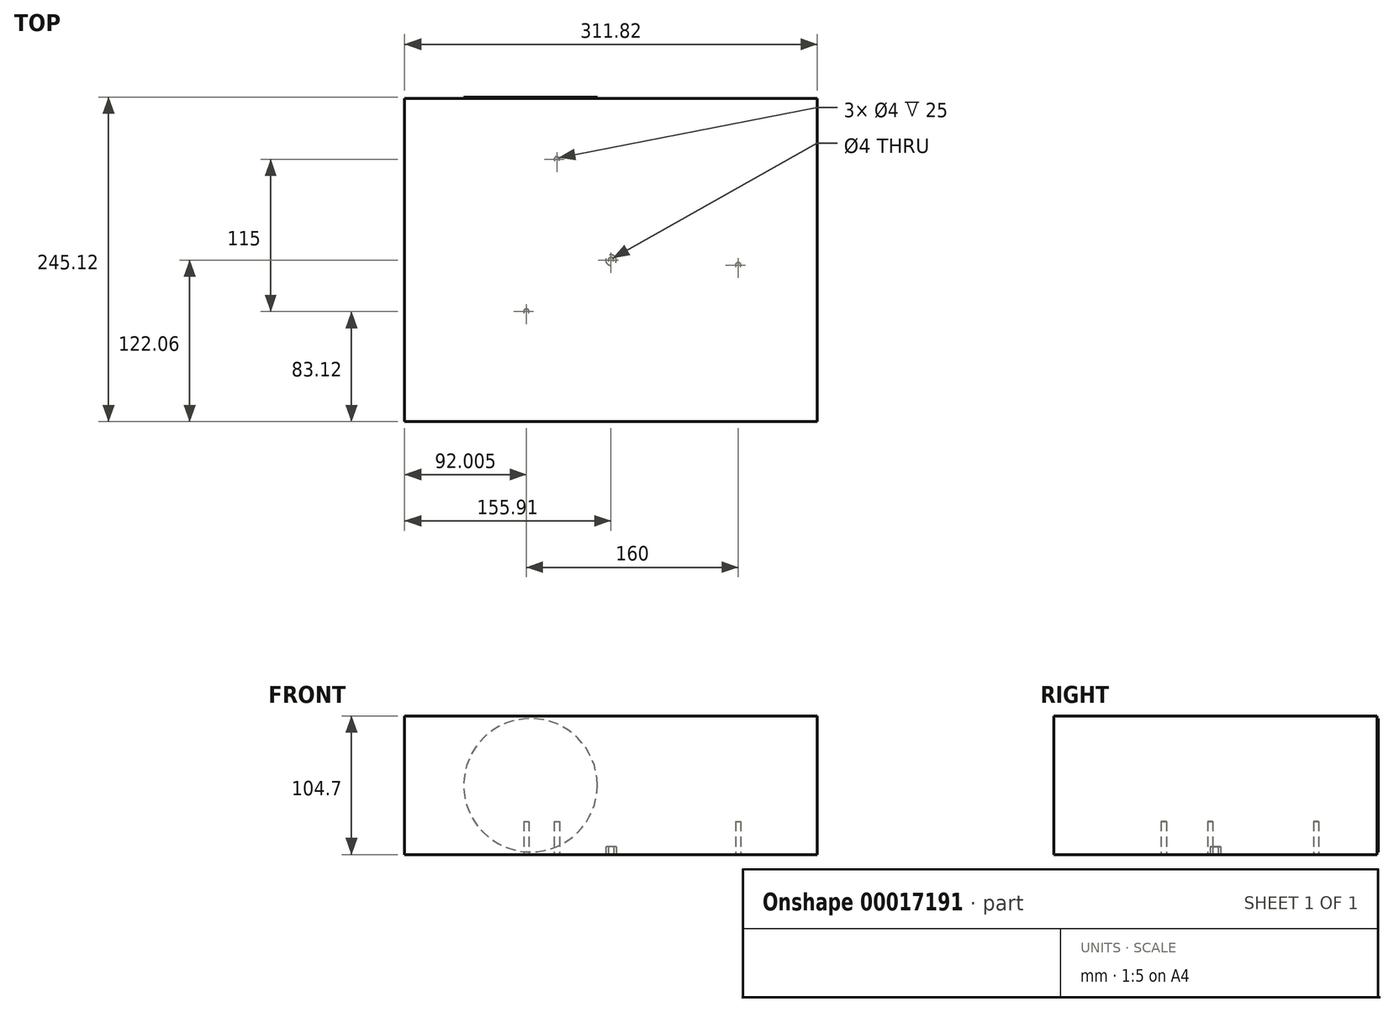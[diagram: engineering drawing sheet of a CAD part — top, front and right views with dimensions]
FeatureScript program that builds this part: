
annotation { "Feature Type Name" : "Feature", "Feature Type Description" : "" }
export const myFeature = defineFeature(function(context is Context, id is Id, definition is map)
    precondition{}
    {
        {
            var Q0;
            Q0=qCreatedBy(makeId("Top.planeOp"),FACE);
            var sketch = newSketch(context, id + "F0", { "sketchPlane" : qUnion([Q0])});
            skLineSegment(sketch, "E0.rect.bottom", {"start": v(155.9, -122.06) * mm, "end": v(-155.9, -122.06) * mm});
            skLineSegment(sketch, "E0.rect.top", {"start": v(155.9, 122.06) * mm, "end": v(-155.9, 122.06) * mm});
            skLineSegment(sketch, "E0.rect.left", {"start": v(155.9, -122.06) * mm, "end": v(155.9, 122.06) * mm});
            skLineSegment(sketch, "E0.rect.right", {"start": v(-155.9, -122.06) * mm, "end": v(-155.9, 122.06) * mm});
            skPoint(sketch, "E0.rect.middle", {"position": v(0, 0) * mm});
            skSolve(sketch);
        }
        {
            var Q0;
            Q0=qSketchRegion(id+"F0",true);
            extrude(context, id + "F1", {"entities" : qUnion([Q0]), "depth" : 104.7 * mm});
        }
        {
            var Q0;
            Q0=makeQuery(id+"F1.opExtrude","SWEPT_FACE",FACE,{"disambiguationData":[OSD([sQuery(id+"F0.wireOp",EDGE,"E0.rect.top")])]});
            var sketch = newSketch(context, id + "F2", { "sketchPlane" : qUnion([Q0])});
            skCircle(sketch, "E1", {"center": v(60.78, 52.35) * mm, "radius": 50.41 * mm});
            skLineSegment(sketch, "E2", {"start": v(155.9, 52.35) * mm, "end": v(85.38, 52.35) * mm, "construction": true});
            skSolve(sketch);
        }
        {
            var Q0;
            Q0=qSketchRegion(id+"F2",true);
            extrude(context, id + "F3", {"entities" : qUnion([Q0]), "operationType" : NewBodyOperationType.ADD, "depth" : 1 * mm});
        }
        {
            var Q0;
            Q0=makeQuery(id+"F1.opExtrude","CAP_FACE",FACE,{"disambiguationData":[OSD([sQuery(id+"F0.wireOp",EDGE,"E0.rect.bottom"),sQuery(id+"F0.wireOp",EDGE,"E0.rect.top"),sQuery(id+"F0.wireOp",EDGE,"E0.rect.left"),sQuery(id+"F0.wireOp",EDGE,"E0.rect.right")])],"isStart":true});
            var sketch = newSketch(context, id + "F4", { "sketchPlane" : qUnion([Q0])});
            skCircle(sketch, "E3", {"center": v(-63.9, 38.94) * mm, "radius": 2 * mm});
            skCircle(sketch, "E4", {"center": v(96.1, 3.94) * mm, "radius": 2 * mm});
            skCircle(sketch, "E5", {"center": v(-40.9, -76.06) * mm, "radius": 2 * mm});
            skLineSegment(sketch, "E6", {"start": v(12.69, 45.56) * mm, "end": v(12.69, -41.44) * mm, "construction": true});
            skLineSegment(sketch, "E7", {"start": v(45.1, -10.78) * mm, "end": v(-17.73, -10.78) * mm, "construction": true});
            skSolve(sketch);
        }
        {
            var Q0;
            Q0=qSketchRegion(id+"F4",true);
            extrude(context, id + "F5", {"entities" : qUnion([Q0]), "operationType" : NewBodyOperationType.REMOVE, "oppositeDirection" : true, "depth" : 25 * mm});
        }
        {
            var Q0;
            Q0=qCreatedBy(makeId("Top.planeOp"),FACE);
            var sketch = newSketch(context, id + "F6", { "sketchPlane" : qUnion([Q0])});
            skCircle(sketch, "E8", {"center": v(0, 0) * mm, "radius": 2 * mm});
            skCircle(sketch, "E9", {"center": v(0, 0) * mm, "radius": 4 * mm});
            skSolve(sketch);
        }
        {
            var Q0;
            Q0=qSketchRegion(id+"F6",true);
            extrude(context, id + "F7", {"entities" : qUnion([Q0]), "depth" : 6 * mm});
        }
    });
